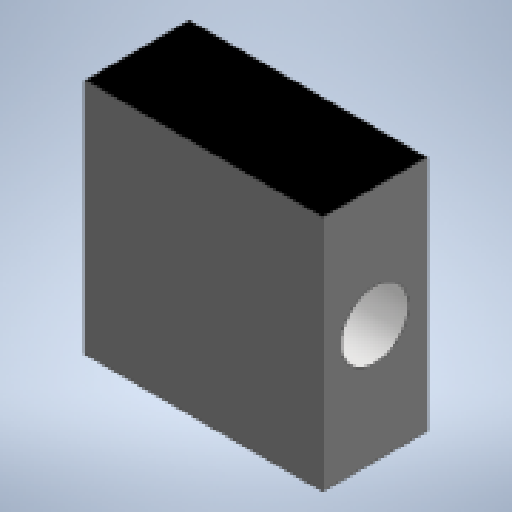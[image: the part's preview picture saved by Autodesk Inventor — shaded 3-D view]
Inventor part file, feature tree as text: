
AUTODESK INVENTOR PART (.ipt)
format: ipt  version: 2023 (Build 270158000, 158)  size: 196,608 bytes
history: native  units: in
note: dims shown in document units (in); Inventor stores cm internally (conversion verified against a paired STEP export)
features: extrude x2, sketch x2
ambient origin geometry x8: Origin, YZ Plane, XZ Plane, XY Plane, X Axis, Y Axis, Z Axis, Center Point
bodies: Solid1 (feature_tree)
feature tree (4):
  extrude  "Extrusion1"  Depth=1.2598in
  extrude  "Extrusion2"  Depth=0.5512in
  sketch  "Sketch1"  dims[d0=1.2598in d1=1.2598in]
  sketch  "Sketch2"  dims[d2=0.5512in d3=0.0in d4=0.3543in d5=0.0in d6=0.0in]
